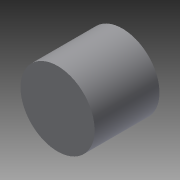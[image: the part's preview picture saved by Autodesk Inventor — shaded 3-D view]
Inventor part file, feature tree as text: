
AUTODESK INVENTOR PART (.ipt)
format: ipt  version: 2015 (Build 190159000, 159)  size: 84,992 bytes
history: native  units: mm
features: extrude x2, sketch x2
ambient origin geometry x8: Origin, YZ Plane, XZ Plane, XY Plane, X Axis, Y Axis, Z Axis, Center Point
bodies: Solid1 (feature_tree)
feature tree (4):
  extrude  "Extrusion1"  Depth=7.0mm TaperAngle=0.0deg
  extrude  "Extrusion2"  Depth=5.0mm
  sketch  "Sketch1"  dims[d0=8.0mm d1=7.0mm d2=0.0mm]
  sketch  "Sketch2"  dims[d3=3.22mm d4=1.61mm d6=1.61mm d7=5.0mm d8=0.0mm]
